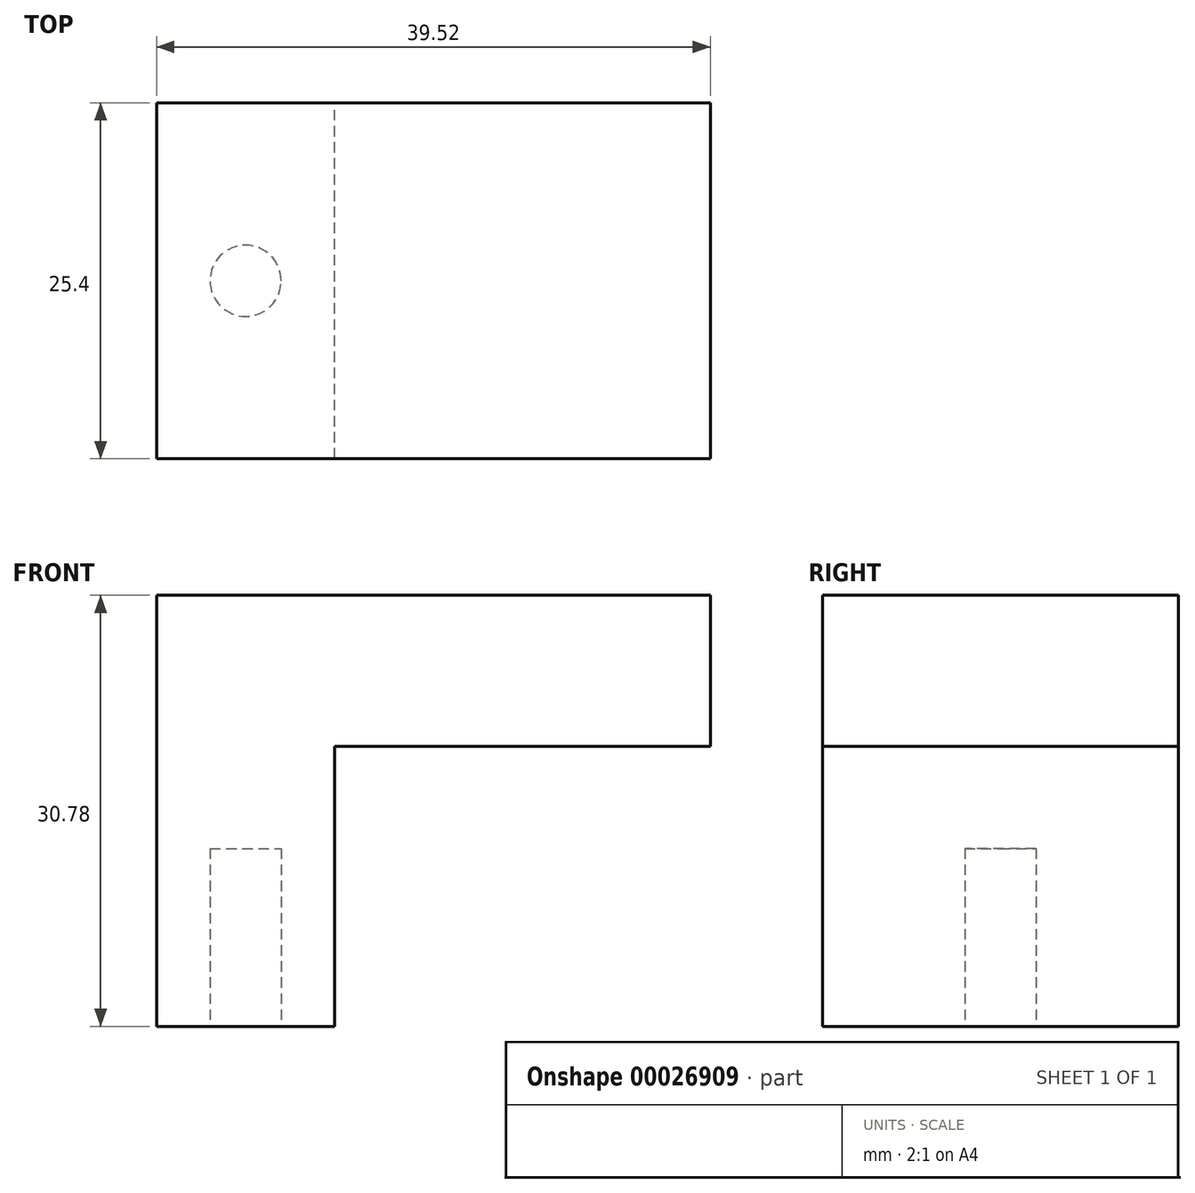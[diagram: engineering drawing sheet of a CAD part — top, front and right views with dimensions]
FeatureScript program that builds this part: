
annotation { "Feature Type Name" : "Feature", "Feature Type Description" : "" }
export const myFeature = defineFeature(function(context is Context, id is Id, definition is map)
    precondition{}
    {
        {
            var Q0;
            Q0=qCreatedBy(makeId("Front.planeOp"),FACE);
            var sketch = newSketch(context, id + "F0", { "sketchPlane" : qUnion([Q0])});
            skLineSegment(sketch, "E0.bottom", {"start": v(-37.9, 10.35) * mm, "end": v(-25.2, 10.35) * mm});
            skLineSegment(sketch, "E0.top", {"start": v(-37.9, 41.13) * mm, "end": v(-25.2, 41.13) * mm});
            skLineSegment(sketch, "E0.left", {"start": v(-37.9, 10.35) * mm, "end": v(-37.9, 41.13) * mm});
            skLineSegment(sketch, "E0.right", {"start": v(-25.2, 10.35) * mm, "end": v(-25.2, 41.13) * mm});
            skLineSegment(sketch, "E1.bottom", {"start": v(-25.2, 41.13) * mm, "end": v(1.63, 41.13) * mm});
            skLineSegment(sketch, "E1.top", {"start": v(-25.2, 30.33) * mm, "end": v(1.63, 30.33) * mm});
            skLineSegment(sketch, "E1.left", {"start": v(-25.2, 41.13) * mm, "end": v(-25.2, 30.33) * mm});
            skLineSegment(sketch, "E1.right", {"start": v(1.63, 41.13) * mm, "end": v(1.63, 30.33) * mm});
            skSolve(sketch);
        }
        {
            var Q0;
            Q0=makeQuery(id+"F0.imprint","IMPRINT",FACE,{"disambiguationData":[TD([[makeQuery(id+"F0.imprint","IMPRINT",EDGE,{"derivedFrom":sQuery(id+"F0.wireOp",EDGE,"E0.bottom")}),1.0]])]});
            var Q1;
            Q1=makeQuery(id+"F0.imprint","IMPRINT",FACE,{"disambiguationData":[TD([[makeQuery(id+"F0.imprint","IMPRINT",EDGE,{"derivedFrom":sQuery(id+"F0.wireOp",EDGE,"E1.bottom")}),-1.0]])]});
            extrude(context, id + "F1", {"entities" : qUnion([Q0, Q1]), "depth" : 25.4 * mm});
        }
        {
            var Q0;
            Q0=makeQuery(id+"F1.opExtrude","SWEPT_FACE",FACE,{"disambiguationData":[OSD([sQuery(id+"F0.wireOp",EDGE,"E0.bottom")])]});
            var sketch = newSketch(context, id + "F2", { "sketchPlane" : qUnion([Q0])});
            skCircle(sketch, "E2", {"center": v(-31.54, 12.7) * mm, "radius": 2.54 * mm});
            skSolve(sketch);
        }
        {
            var Q0;
            Q0=makeQuery(id+"F2.imprint","IMPRINT",FACE,{"disambiguationData":[TD([[makeQuery(id+"F2.imprint","IMPRINT",EDGE,{"derivedFrom":sQuery(id+"F2.wireOp",EDGE,"E2")}),1.0]])]});
            extrude(context, id + "F3", {"entities" : qUnion([Q0]), "operationType" : NewBodyOperationType.REMOVE, "oppositeDirection" : true, "depth" : 12.7 * mm});
        }
    });
